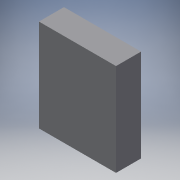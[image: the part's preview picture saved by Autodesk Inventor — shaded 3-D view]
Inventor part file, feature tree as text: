
AUTODESK INVENTOR PART (.ipt)
format: ipt  version: 2016 (Build 200138000, 138)  size: 83,968 bytes
history: native  units: mm
features: extrude x1, sketch x1
ambient origin geometry x8: Origin, YZ Plane, XZ Plane, XY Plane, X Axis, Y Axis, Z Axis, Center Point
bodies: Solid1 (feature_tree)
feature tree (2):
  extrude  "Extrusion1"  [1 undecoded]
  sketch  "Sketch1"  dims[d3=0.0mm]
note: 1 required parameter value undecoded (feature->parameter linkage not recoverable at this tier; creation-order binding heuristic only, values carry confidence <= 0.55)
